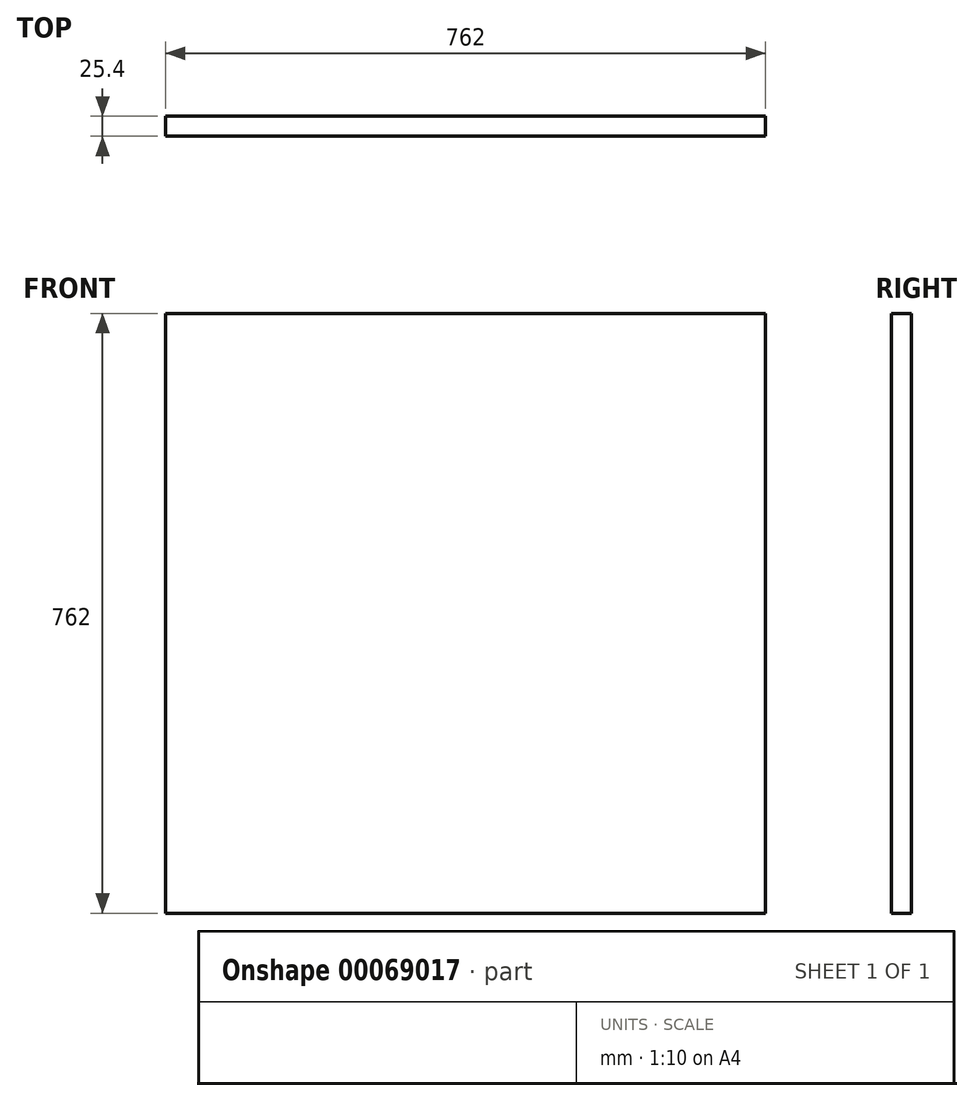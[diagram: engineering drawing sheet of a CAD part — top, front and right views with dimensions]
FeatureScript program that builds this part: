
annotation { "Feature Type Name" : "Feature", "Feature Type Description" : "" }
export const myFeature = defineFeature(function(context is Context, id is Id, definition is map)
    precondition{}
    {
        {
            var Q0;
            Q0=qCreatedBy(makeId("Front.planeOp"),FACE);
            var sketch = newSketch(context, id + "F0", { "sketchPlane" : qUnion([Q0])});
            skLineSegment(sketch, "E0.bottom", {"start": v(-762, 762) * mm, "end": v(0, 762) * mm});
            skLineSegment(sketch, "E0.top", {"start": v(-762, 0) * mm, "end": v(0, 0) * mm});
            skLineSegment(sketch, "E0.left", {"start": v(-762, 762) * mm, "end": v(-762, 0) * mm});
            skLineSegment(sketch, "E0.right", {"start": v(0, 762) * mm, "end": v(0, 0) * mm});
            skSolve(sketch);
        }
        {
            var Q0;
            Q0=makeQuery(id+"F0.imprint","IMPRINT",FACE,{"disambiguationData":[TD([[makeQuery(id+"F0.imprint","IMPRINT",EDGE,{"derivedFrom":sQuery(id+"F0.wireOp",EDGE,"E0.bottom")}),-1.0]])]});
            extrude(context, id + "F1", {"entities" : qUnion([Q0]), "depth" : 25.4 * mm});
        }
    });
